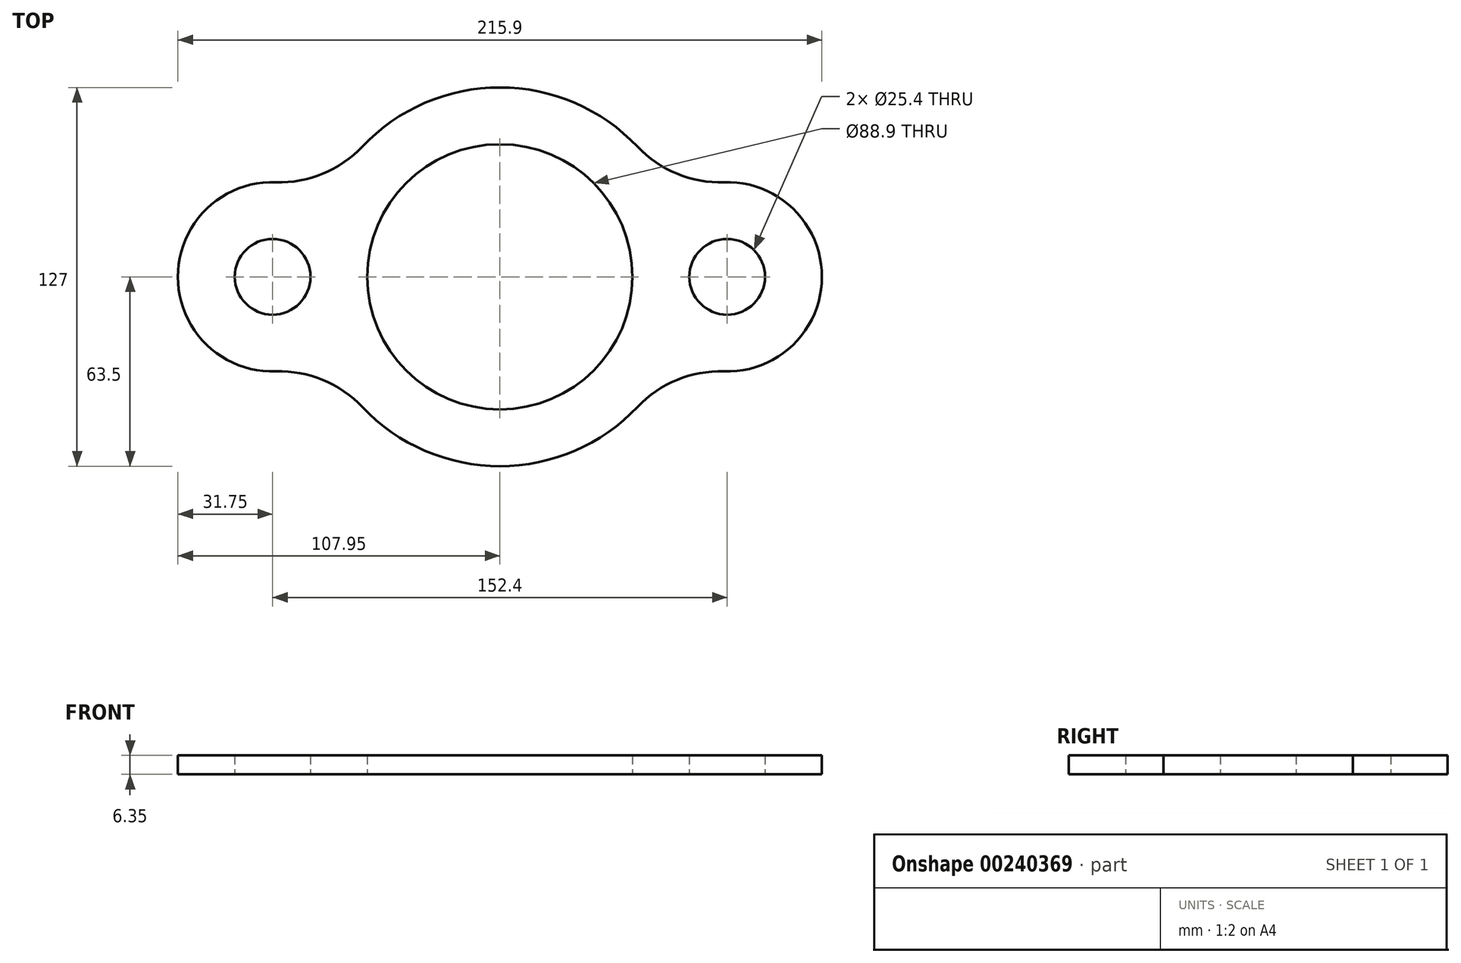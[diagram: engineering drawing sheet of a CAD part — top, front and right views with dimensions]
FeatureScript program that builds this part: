
annotation { "Feature Type Name" : "Feature", "Feature Type Description" : "" }
export const myFeature = defineFeature(function(context is Context, id is Id, definition is map)
    precondition{}
    {
        {
            var Q0;
            Q0=qCreatedBy(makeId("Top.planeOp"),FACE);
            var sketch = newSketch(context, id + "F0", { "sketchPlane" : qUnion([Q0])});
            skCircle(sketch, "E0", {"center": v(0, 0) * mm, "radius": 44.45 * mm});
            skArc(sketch, "E1", {"start": v(-46.14, -43.63) * mm, "mid": v(0, -63.5) * mm, "end": v(46.14, -43.63) * mm});
            skCircle(sketch, "E2", {"center": v(-76.2, 0) * mm, "radius": 12.7 * mm});
            skArc(sketch, "E3", {"start": v(-75.12, 31.73) * mm, "mid": v(-107.95, 0) * mm, "end": v(-75.12, -31.73) * mm});
            skCircle(sketch, "E4", {"center": v(76.2, 0) * mm, "radius": 12.7 * mm});
            skArc(sketch, "E5", {"start": v(75.12, -31.73) * mm, "mid": v(107.95, 0) * mm, "end": v(75.12, 31.73) * mm});
            skArc(sketch, "E6", {"start": v(46.14, 43.63) * mm, "mid": v(59.35, 34.56) * mm, "end": v(75.12, 31.73) * mm});
            skArc(sketch, "E7", {"start": v(-75.12, 31.73) * mm, "mid": v(-59.35, 34.56) * mm, "end": v(-46.14, 43.63) * mm});
            skArc(sketch, "E8", {"start": v(-46.14, -43.63) * mm, "mid": v(-59.35, -34.56) * mm, "end": v(-75.12, -31.73) * mm});
            skArc(sketch, "E9", {"start": v(75.12, -31.73) * mm, "mid": v(59.35, -34.56) * mm, "end": v(46.14, -43.63) * mm});
            skArc(sketch, "E10.trimOffspring", {"start": v(46.14, 43.63) * mm, "mid": v(0, 63.5) * mm, "end": v(-46.14, 43.63) * mm});
            skSolve(sketch);
        }
        {
            var Q0;
            Q0 = qSketchRegion(id + "F0", true);
            extrude(context, id + "F1", {"entities" : qUnion([Q0]), "depth" : 6.35 * mm});
        }
    });
